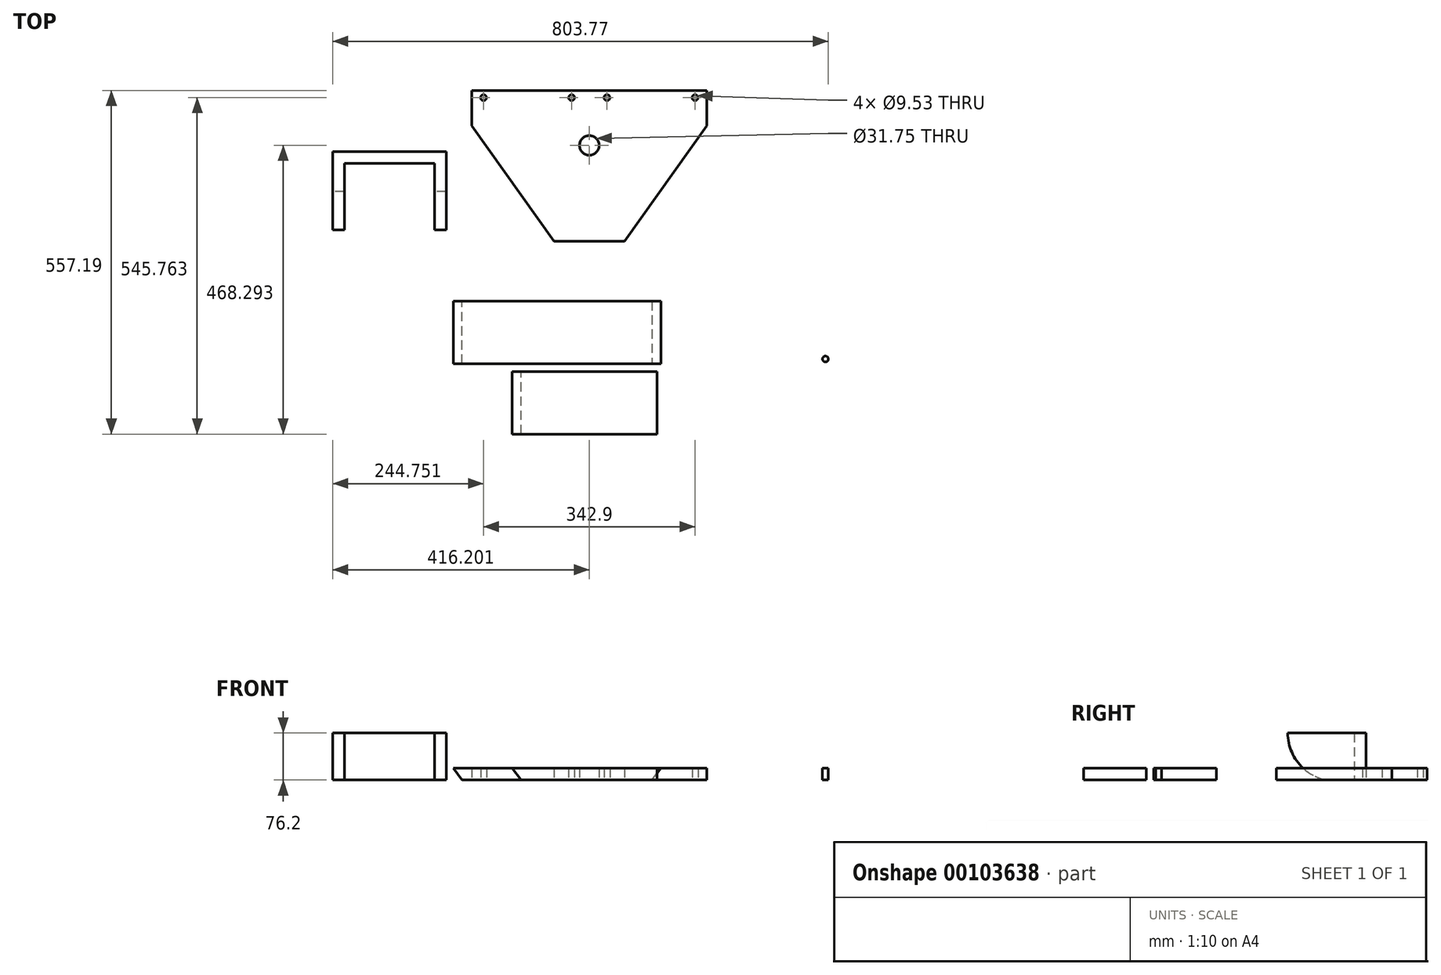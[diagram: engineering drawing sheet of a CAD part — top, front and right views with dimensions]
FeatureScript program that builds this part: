
annotation { "Feature Type Name" : "Feature", "Feature Type Description" : "" }
export const myFeature = defineFeature(function(context is Context, id is Id, definition is map)
    precondition{}
    {
        {
            var Q0;
            Q0=qCreatedBy(makeId("Top.planeOp"),FACE);
            var sketch = newSketch(context, id + "F0", { "sketchPlane" : qUnion([Q0])});
            skLineSegment(sketch, "E0", {"start": v(-181.4, 47.7) * mm, "end": v(155.14, 47.7) * mm});
            skLineSegment(sketch, "E1", {"start": v(155.14, 47.7) * mm, "end": v(155.14, -53.9) * mm});
            skLineSegment(sketch, "E2", {"start": v(155.14, -53.9) * mm, "end": v(-181.4, -53.9) * mm});
            skLineSegment(sketch, "E3", {"start": v(-181.4, 47.7) * mm, "end": v(-181.4, -53.9) * mm});
            skSolve(sketch);
        }
        {
            var Q0;
            Q0=makeQuery(id+"F0.imprint","IMPRINT",FACE,{"disambiguationData":[TD([[makeQuery(id+"F0.imprint","IMPRINT",EDGE,{"derivedFrom":sQuery(id+"F0.wireOp",EDGE,"E0")}),-1.0]])]});
            extrude(context, id + "F1", {"entities" : qUnion([Q0]), "depth" : 19.05 * mm});
        }
        {
            var Q0;
            Q0=makeQuery(id+"F1.opExtrude","CAP_EDGE",EDGE,{"disambiguationData":[OSD([sQuery(id+"F0.wireOp",EDGE,"E3")])],"isStart":true});
            var Q1;
            Q1=makeQuery(id+"F1.opExtrude","CAP_EDGE",EDGE,{"disambiguationData":[OSD([sQuery(id+"F0.wireOp",EDGE,"E1")])],"isStart":true});
            chamfer(context, id + "F2", {"entities" : qUnion([Q0, Q1]), "chamferType" : ChamferType.OFFSET_ANGLE, "width" : 19.05 * mm, "oppositeDirection" : false, "angle" : 37 * degree, "tangentPropagation" : true});
        }
        {
            var Q0;
            Q0=qCreatedBy(makeId("Top.planeOp"),FACE);
            var sketch = newSketch(context, id + "F3", { "sketchPlane" : qUnion([Q0])});
            skLineSegment(sketch, "E4.bottom", {"start": v(-85.9, -66.35) * mm, "end": v(149.05, -66.35) * mm});
            skLineSegment(sketch, "E4.top", {"start": v(-85.9, -167.95) * mm, "end": v(149.05, -167.95) * mm});
            skLineSegment(sketch, "E4.left", {"start": v(-85.9, -66.35) * mm, "end": v(-85.9, -167.95) * mm});
            skLineSegment(sketch, "E4.right", {"start": v(149.05, -66.35) * mm, "end": v(149.05, -167.95) * mm});
            skSolve(sketch);
        }
        {
            var Q0;
            Q0=makeQuery(id+"F3.imprint","IMPRINT",FACE,{"disambiguationData":[TD([[makeQuery(id+"F3.imprint","IMPRINT",EDGE,{"derivedFrom":sQuery(id+"F3.wireOp",EDGE,"E4.bottom")}),-1.0]])]});
            extrude(context, id + "F4", {"entities" : qUnion([Q0]), "depth" : 19.05 * mm});
        }
        {
            var Q0;
            Q0=makeQuery(id+"F4.opExtrude","CAP_EDGE",EDGE,{"disambiguationData":[OSD([sQuery(id+"F3.wireOp",EDGE,"E4.left")])],"isStart":true});
            chamfer(context, id + "F5", {"entities" : qUnion([Q0]), "chamferType" : ChamferType.OFFSET_ANGLE, "width" : 19.05 * mm, "oppositeDirection" : false, "angle" : 37 * degree, "tangentPropagation" : true});
        }
        {
            var Q0;
            Q0=qCreatedBy(makeId("Top.planeOp"),FACE);
            var sketch = newSketch(context, id + "F6", { "sketchPlane" : qUnion([Q0])});
            skLineSegment(sketch, "E5", {"start": v(-151.45, 389.24) * mm, "end": v(229.55, 389.24) * mm});
            skLineSegment(sketch, "E6", {"start": v(229.55, 389.24) * mm, "end": v(229.55, 332.1) * mm});
            skLineSegment(sketch, "E7", {"start": v(39.05, 389.24) * mm, "end": v(39.05, 107.56) * mm, "construction": true});
            skLineSegment(sketch, "E8", {"start": v(-151.45, 389.24) * mm, "end": v(-151.45, 332.1) * mm});
            skCircle(sketch, "E9", {"center": v(39.05, 300.34) * mm, "radius": 15.88 * mm});
            skLineSegment(sketch, "E10", {"start": v(-18.1, 144.77) * mm, "end": v(96.2, 144.77) * mm});
            skLineSegment(sketch, "E11", {"start": v(-151.45, 332.1) * mm, "end": v(-18.1, 144.77) * mm});
            skLineSegment(sketch, "E12", {"start": v(96.2, 144.77) * mm, "end": v(229.55, 332.1) * mm});
            skCircle(sketch, "E13", {"center": v(-132.4, 377.81) * mm, "radius": 4.76 * mm});
            skCircle(sketch, "E14", {"center": v(10.35, 377.81) * mm, "radius": 4.76 * mm});
            skCircle(sketch, "E15.0.MirrorC", {"center": v(210.5, 377.81) * mm, "radius": 4.76 * mm});
            skCircle(sketch, "E15.1.MirrorC", {"center": v(67.75, 377.81) * mm, "radius": 4.76 * mm});
            skSolve(sketch);
        }
        {
            var Q0;
            Q0=makeQuery(id+"F6.imprint","IMPRINT",FACE,{"disambiguationData":[TD([[makeQuery(id+"F6.imprint","IMPRINT",EDGE,{"derivedFrom":sQuery(id+"F6.wireOp",EDGE,"E5")}),-1.0]])]});
            extrude(context, id + "F7", {"entities" : qUnion([Q0]), "depth" : 19.05 * mm});
        }
        {
            var Q0;
            Q0=qCreatedBy(makeId("Top.planeOp"),FACE);
            var sketch = newSketch(context, id + "F8", { "sketchPlane" : qUnion([Q0])});
            skLineSegment(sketch, "E16.bottom", {"start": v(-377.15, 290.21) * mm, "end": v(-193, 290.21) * mm});
            skLineSegment(sketch, "E16.top", {"start": v(-358.1, 271.16) * mm, "end": v(-212.05, 271.16) * mm});
            skLineSegment(sketch, "E16.left", {"start": v(-377.15, 290.21) * mm, "end": v(-377.15, 271.16) * mm});
            skLineSegment(sketch, "E16.right", {"start": v(-193, 290.21) * mm, "end": v(-193, 271.16) * mm});
            skLineSegment(sketch, "E17.top", {"start": v(-377.15, 163.21) * mm, "end": v(-358.1, 163.21) * mm});
            skLineSegment(sketch, "E17.left", {"start": v(-377.15, 271.16) * mm, "end": v(-377.15, 163.21) * mm});
            skLineSegment(sketch, "E17.right", {"start": v(-358.1, 271.16) * mm, "end": v(-358.1, 163.21) * mm});
            skLineSegment(sketch, "E18.top", {"start": v(-193, 163.21) * mm, "end": v(-212.05, 163.21) * mm});
            skLineSegment(sketch, "E18.left", {"start": v(-193, 271.16) * mm, "end": v(-193, 163.21) * mm});
            skLineSegment(sketch, "E18.right", {"start": v(-212.05, 271.16) * mm, "end": v(-212.05, 163.21) * mm});
            skSolve(sketch);
        }
        {
            var Q0;
            Q0=makeQuery(id+"F8.imprint","IMPRINT",FACE,{"disambiguationData":[TD([[makeQuery(id+"F8.imprint","IMPRINT",EDGE,{"derivedFrom":sQuery(id+"F8.wireOp",EDGE,"E16.bottom")}),-1.0]])]});
            extrude(context, id + "F9", {"entities" : qUnion([Q0]), "depth" : 76.2 * mm});
        }
        {
            var Q0;
            Q0=makeQuery(id+"F9.opExtrude","SWEPT_FACE",FACE,{"disambiguationData":[OSD([sQuery(id+"F8.wireOp",EDGE,"E16.left")])]});
            var sketch = newSketch(context, id + "F10", { "sketchPlane" : qUnion([Q0])});
            skArc(sketch, "E19", {"start": v(-225.72, 0) * mm, "mid": v(-180.84, 26.92) * mm, "end": v(-163.21, 76.2) * mm});
            skLineSegment(sketch, "E20", {"start": v(-163.21, 76.2) * mm, "end": v(-163.21, 0) * mm});
            skLineSegment(sketch, "E21", {"start": v(-163.21, 0) * mm, "end": v(-225.72, 0) * mm});
            skSolve(sketch);
        }
        {
            var Q0;
            Q0=makeQuery(id+"F10.imprint","IMPRINT",FACE,{"disambiguationData":[TD([[makeQuery(id+"F10.imprint","IMPRINT",EDGE,{"derivedFrom":sQuery(id+"F10.wireOp",EDGE,"E19")}),-1.0]])]});
            extrude(context, id + "F11", {"entities" : qUnion([Q0]), "operationType" : NewBodyOperationType.REMOVE, "oppositeDirection" : true, "depth" : 190.5 * mm});
        }
        {
            var Q0;
            Q0=qCreatedBy(makeId("Top.planeOp"),FACE);
            var sketch = newSketch(context, id + "F12", { "sketchPlane" : qUnion([Q0])});
            skLineSegment(sketch, "E22.bottom", {"start": v(179.4, 149.93) * mm, "end": v(463.88, 149.93) * mm});
            skLineSegment(sketch, "E23", {"start": v(463.88, 149.93) * mm, "end": v(431.73, -84.44) * mm});
            skLineSegment(sketch, "E24", {"start": v(179.4, 149.93) * mm, "end": v(211.54, -84.44) * mm});
            skArc(sketch, "E25", {"start": v(211.54, -84.44) * mm, "mid": v(321.64, -180.46) * mm, "end": v(431.73, -84.44) * mm});
            skLineSegment(sketch, "E26.rect.bottom", {"start": v(321.64, -167.57) * mm, "end": v(321.64, -167.57) * mm});
            skLineSegment(sketch, "E26.rect.top", {"start": v(321.64, 111.83) * mm, "end": v(321.64, 111.83) * mm});
            skLineSegment(sketch, "E26.rect.left", {"start": v(329.9, -159.32) * mm, "end": v(329.9, 103.57) * mm});
            skLineSegment(sketch, "E26.rect.right", {"start": v(313.38, -159.32) * mm, "end": v(313.38, 103.57) * mm});
            skPoint(sketch, "E26.rect.middle", {"position": v(321.64, -27.87) * mm});
            skPoint(sketch, "E27.visualSharp", {"position": v(313.38, 111.83) * mm});
            skArc(sketch, "E27.filletArc", {"start": v(321.64, 111.83) * mm, "mid": v(315.8, 109.4) * mm, "end": v(313.38, 103.57) * mm});
            skPoint(sketch, "E28.visualSharp", {"position": v(329.9, 111.83) * mm});
            skArc(sketch, "E28.filletArc", {"start": v(329.9, 103.57) * mm, "mid": v(327.48, 109.4) * mm, "end": v(321.64, 111.83) * mm});
            skPoint(sketch, "E29.visualSharp", {"position": v(313.38, -167.57) * mm});
            skArc(sketch, "E29.filletArc", {"start": v(313.38, -159.32) * mm, "mid": v(315.8, -165.16) * mm, "end": v(321.64, -167.57) * mm});
            skPoint(sketch, "E30.visualSharp", {"position": v(329.9, -167.57) * mm});
            skArc(sketch, "E30.filletArc", {"start": v(321.64, -167.57) * mm, "mid": v(327.48, -165.16) * mm, "end": v(329.9, -159.32) * mm});
            skSolve(sketch);
        }
        {
            var Q0;
            Q0=qSketchRegion(id+"F12",true);
            extrude(context, id + "F13", {"entities" : qUnion([Q0]), "depth" : 19.05 * mm});
        }
        {
            var Q0;
            Q0=makeQuery(id+"F13.opExtrude","CAP_FACE",FACE,{"disambiguationData":[OSD([sQuery(id+"F12.wireOp",EDGE,"E22.bottom"),sQuery(id+"F12.wireOp",EDGE,"E23"),sQuery(id+"F12.wireOp",EDGE,"E24"),sQuery(id+"F12.wireOp",EDGE,"E25"),sQuery(id+"F12.wireOp",EDGE,"E26.rect.left"),sQuery(id+"F12.wireOp",EDGE,"E26.rect.right"),sQuery(id+"F12.wireOp",EDGE,"E27.filletArc"),sQuery(id+"F12.wireOp",EDGE,"E28.filletArc"),sQuery(id+"F12.wireOp",EDGE,"E29.filletArc"),sQuery(id+"F12.wireOp",EDGE,"E30.filletArc")])],"isStart":false});
            var sketch = newSketch(context, id + "F14", { "sketchPlane" : qUnion([Q0])});
            skCircle(sketch, "E31", {"center": v(221.42, -46.16) * mm, "radius": 4.76 * mm});
            skLineSegment(sketch, "E32", {"start": v(321.64, 111.83) * mm, "end": v(321.64, -151.06) * mm, "construction": true});
            skCircle(sketch, "E33.0.MirrorC", {"center": v(421.86, -46.16) * mm, "radius": 4.76 * mm});
            skSolve(sketch);
        }
        {
            var Q0;
            {Q0=qUnion([makeQuery(id+"F14.imprint","IMPRINT",FACE,{"disambiguationData":[TD([[makeQuery(id+"F14.imprint","IMPRINT",EDGE,{"derivedFrom":sQuery(id+"F14.wireOp",EDGE,"E31")}),1.0]])]}),makeQuery(id+"F14.imprint","IMPRINT",FACE,{"disambiguationData":[TD([[makeQuery(id+"F14.imprint","IMPRINT",EDGE,{"derivedFrom":sQuery(id+"F14.wireOp",EDGE,"E33.0.MirrorC")}),-1.0]])]})]);}
            extrude(context, id + "F15", {"entities" : qUnion([Q0]), "operationType" : NewBodyOperationType.REMOVE, "endBound" : BoundingType.THROUGH_ALL, "oppositeDirection" : true, "depth" : 25.4 * mm});
        }
    });
